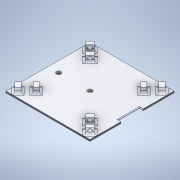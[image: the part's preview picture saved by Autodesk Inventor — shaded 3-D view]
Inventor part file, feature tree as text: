
AUTODESK INVENTOR PART (.ipt)
format: ipt  version: 2022 (Build 260153000, 153)  size: 320,512 bytes
history: native  units: in
note: dims shown in document units (in); Inventor stores cm internally (conversion verified against a paired STEP export)
features: sketch x7, extrude x4, hole x3, fillet x2, chamfer x1, pattern_circular x1
ambient origin geometry x8: Origin, YZ Plane, XZ Plane, XY Plane, X Axis, Y Axis, Z Axis, Center Point
bodies: Solid1 (feature_tree)
feature tree (18):
  extrude  "Extrusion1"  Depth=2.9528in
  hole  "Hole2"  [1 undecoded]
  chamfer  "Chamfer1"  Distance=0.0787in Angle=45.0deg
  hole  "Hole5"  [1 undecoded]
  extrude  "Extrusion5"  Depth=0.2165in
  fillet  "Fillet3"  Radius=0.1575in
  hole  "Hole7"  [1 undecoded]
  pattern_circular  "Circular Pattern6"  [2 undecoded]
  extrude  "Extrusion6"  Depth=0.0197in
  extrude  "Extrusion7"  Depth=0.0197in
  fillet  "Fillet4"  Radius=0.1082in
  sketch  "Sketch1"  dims[d0=2.9528in d1=2.9528in]
  sketch  "Sketch4"  dims[d2=0.1378in d3=0.0in]
  sketch  "Sketch9"  dims[d15=0.1575in d16=0.2362in d17=1.0039in d18=0.0591in d19=90.0deg d20=0.315in d21=0.8108in d22=1.4764in]
  sketch  "Sketch11"  dims[d23=1.4764in d24=0.0787in d25=0.0787in d26=45.0deg]
  sketch  "Sketch13"  dims[d82=0.1575in d83=0.2362in d84=0.1575in d85=0.0787in d86=90.0deg d87=0.315in d88=0.8108in d89=1.1024in]
  sketch  "Sketch14"  dims[d90=1.4764in d97=0.2165in d98=0.1575in]
  sketch  "Sketch15"  dims[d99=0.9276in d100=0.1969in d101=0.0in d102=0.1575in d103=0.2953in d105=0.2165in d106=0.1082in d107=0.0787in d117=0.1181in d118=0.2362in d119=0.1575in d120=0.0787in d121=90.0deg d122=0.315in d123=0.8108in d124=0.1083in d125=0.0787in d129=1.5748in d130=360.0deg d132=0.8661in d133=0.9843in d134=0.9843in d135=0.0433in d136=0.0787in d137=0.0984in d138=0.7874in d140=0.8268in d141=0.7874in d143=0.4921in d146=0.0787in d147=0.0in d148=0.1181in d149=0.7874in d150=0.0984in d151=0.0in d152=0.0in d153=0.0197in d131=0.0197in]
note: 5 required parameter values undecoded (feature->parameter linkage not recoverable at this tier; creation-order binding heuristic only, values carry confidence <= 0.55)
